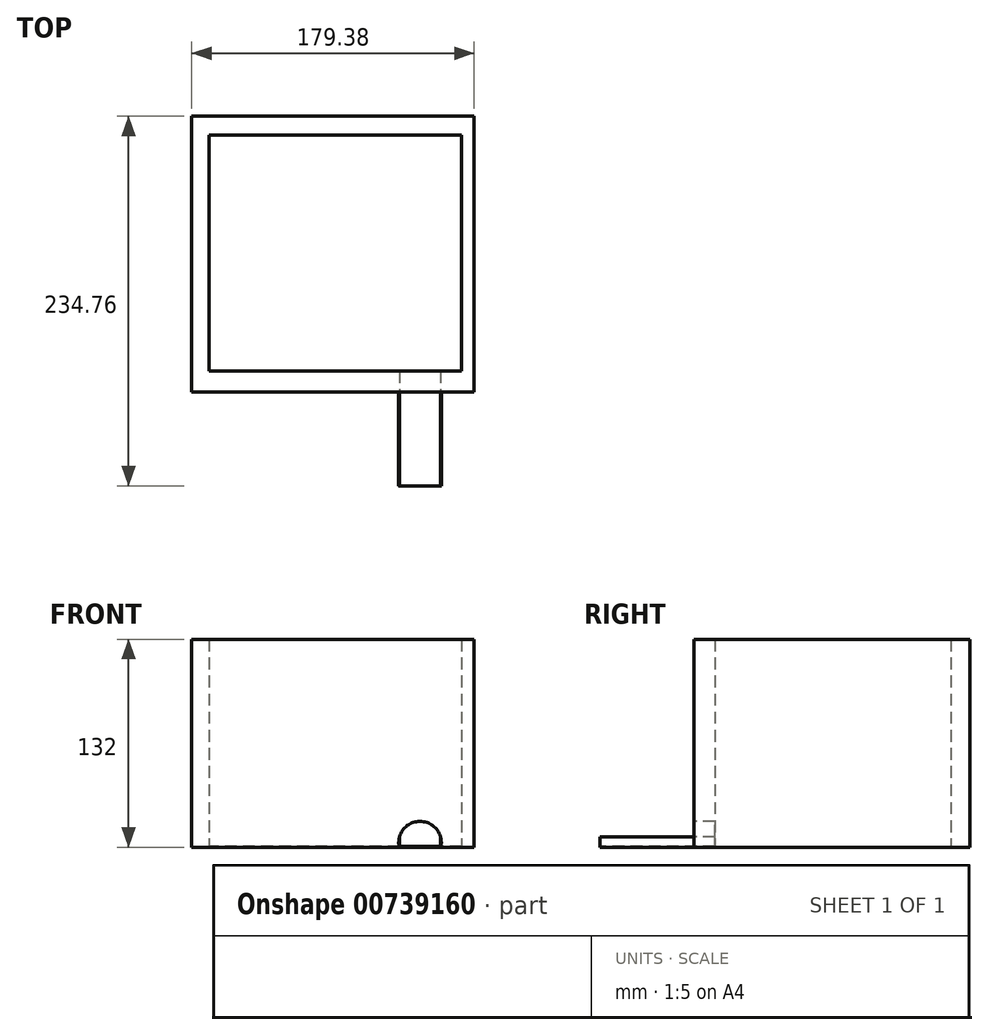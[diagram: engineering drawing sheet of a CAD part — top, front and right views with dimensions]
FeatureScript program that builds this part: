
annotation { "Feature Type Name" : "Feature", "Feature Type Description" : "" }
export const myFeature = defineFeature(function(context is Context, id is Id, definition is map)
    precondition{}
    {
        {
            var Q0;
            Q0=qCreatedBy(makeId("Top.planeOp"),FACE);
            var sketch = newSketch(context, id + "F0", { "sketchPlane" : qUnion([Q0])});
            skLineSegment(sketch, "E0.bottom", {"start": v(-79.21, -70.61) * mm, "end": v(100.17, -70.61) * mm});
            skLineSegment(sketch, "E0.top", {"start": v(-79.21, 104.46) * mm, "end": v(100.17, 104.46) * mm});
            skLineSegment(sketch, "E0.left", {"start": v(-79.21, -70.61) * mm, "end": v(-79.21, 104.46) * mm});
            skLineSegment(sketch, "E0.right", {"start": v(100.17, -70.61) * mm, "end": v(100.17, 104.46) * mm});
            skLineSegment(sketch, "E1.bottom", {"start": v(-68.23, -54.4) * mm, "end": v(92.28, -54.4) * mm});
            skLineSegment(sketch, "E1.top", {"start": v(-68.23, 92.5) * mm, "end": v(92.28, 92.5) * mm});
            skLineSegment(sketch, "E1.left", {"start": v(-68.23, -54.4) * mm, "end": v(-68.23, 92.5) * mm});
            skLineSegment(sketch, "E1.right", {"start": v(92.28, -54.4) * mm, "end": v(92.28, 92.5) * mm});
            skSolve(sketch);
        }
        {
            var Q0;
            Q0=makeQuery(id+"F0.imprint","IMPRINT",FACE,{"disambiguationData":[TD([[makeQuery(id+"F0.imprint","IMPRINT",EDGE,{"derivedFrom":sQuery(id+"F0.wireOp",EDGE,"E0.bottom")}),1.0]])]});
            extrude(context, id + "F1", {"entities" : qUnion([Q0]), "depth" : 132 * mm, "offsetDistance" : 25 * mm});
        }
        {
            var Q0;
            Q0=makeQuery(id+"F1.opExtrude","SWEPT_FACE",FACE,{"disambiguationData":[OSD([sQuery(id+"F0.wireOp",EDGE,"E0.bottom")])]});
            var sketch = newSketch(context, id + "F2", { "sketchPlane" : qUnion([Q0])});
            skArc(sketch, "E2", {"start": v(78.99, 0) * mm, "mid": v(65.79, 16.4) * mm, "end": v(52.59, 0) * mm});
            skSolve(sketch);
        }
        {
            var Q0;
            {var subQ0=sQuery(id+"F2.wireOp",EDGE,"E2");Q0=makeQuery(id+"F2.imprint","IMPRINT",FACE,{"disambiguationData":[TD([[makeQuery(id+"F2.imprint","IMPRINT",EDGE,{"derivedFrom":subQ0}),1.0]])]});}
            extrude(context, id + "F3", {"entities" : qUnion([Q0]), "operationType" : NewBodyOperationType.REMOVE, "oppositeDirection" : true, "depth" : 25 * mm, "offsetDistance" : 25 * mm});
        }
        {
            var Q0;
            Q0=makeQuery(id+"F1.opExtrude","CAP_FACE",FACE,{"disambiguationData":[OSD([sQuery(id+"F0.wireOp",EDGE,"E0.bottom"),sQuery(id+"F0.wireOp",EDGE,"E0.top"),sQuery(id+"F0.wireOp",EDGE,"E0.left"),sQuery(id+"F0.wireOp",EDGE,"E0.right"),sQuery(id+"F0.wireOp",EDGE,"E1.bottom"),sQuery(id+"F0.wireOp",EDGE,"E1.top"),sQuery(id+"F0.wireOp",EDGE,"E1.left"),sQuery(id+"F0.wireOp",EDGE,"E1.right")])],"isStart":true});
            var sketch = newSketch(context, id + "F4", { "sketchPlane" : qUnion([Q0])});
            skLineSegment(sketch, "E3.bottom", {"start": v(-68.23, 54.4) * mm, "end": v(92.28, 54.4) * mm});
            skLineSegment(sketch, "E3.top", {"start": v(-68.23, -92.5) * mm, "end": v(92.28, -92.5) * mm});
            skLineSegment(sketch, "E3.left", {"start": v(-68.23, 54.4) * mm, "end": v(-68.23, -92.5) * mm});
            skLineSegment(sketch, "E3.right", {"start": v(92.28, 54.4) * mm, "end": v(92.28, -92.5) * mm});
            skSolve(sketch);
        }
        {
            var Q0;
            Q0=makeQuery(id+"F4.imprint","IMPRINT",FACE,{"disambiguationData":[TD([[makeQuery(id+"F4.imprint","IMPRINT",EDGE,{"derivedFrom":sQuery(id+"F4.wireOp",EDGE,"E3.top")}),1.0]])]});
            extrude(context, id + "F5", {"entities" : qUnion([Q0]), "operationType" : NewBodyOperationType.ADD, "oppositeDirection" : true, "depth" : 10 * mm, "offsetDistance" : 25 * mm});
        }
        {
            var Q0;
            Q0=makeQuery(id+"F5.opExtrude","CAP_FACE",FACE,{"disambiguationData":[OSD([sQuery(id+"F4.wireOp",EDGE,"E3.bottom"),sQuery(id+"F4.wireOp",EDGE,"E3.top"),sQuery(id+"F4.wireOp",EDGE,"E3.left"),sQuery(id+"F4.wireOp",EDGE,"E3.right")])],"isStart":false});
            extrude(context, id + "F6", {"entities" : qUnion([Q0]), "operationType" : NewBodyOperationType.REMOVE, "oppositeDirection" : true, "depth" : 10 * mm, "offsetDistance" : 25 * mm});
        }
        {
            var Q0;
            Q0=makeQuery(id+"F6.boolean.opBoolean","MERGE",FACE,{"derivedFrom":[makeQuery(id+"F1.opExtrude","SWEPT_FACE",FACE,{"disambiguationData":[OSD([sQuery(id+"F0.wireOp",EDGE,"E1.top")])]}),makeQuery(id+"F6.opExtrude","SWEPT_FACE",FACE,{"disambiguationData":[OSD([sQuery(id+"F4.wireOp",EDGE,"E3.top")])]})]});
            var sketch = newSketch(context, id + "F7", { "sketchPlane" : qUnion([Q0])});
            skLineSegment(sketch, "E4", {"start": v(92.28, 6.67) * mm, "end": v(-68.23, 6.67) * mm});
            skSolve(sketch);
        }
        {
            var Q0;
            Q0 = qSketchRegion(id + "F7", true);
            var Q1;
            {var subQ0=sQuery(id+"F7.wireOp",EDGE,"E4");Q1=makeQuery(id+"F7.imprint","IMPRINT",FACE,{"disambiguationData":[TD([[makeQuery(id+"F7.imprint","IMPRINT",EDGE,{"derivedFrom":subQ0}),1.0]])]});}
            extrude(context, id + "F8", {"entities" : qUnion([Q0, Q1]), "operationType" : NewBodyOperationType.ADD, "depth" : 163 * mm, "offsetDistance" : 25 * mm});
        }
        {
            var Q0;
            Q0=makeQuery(id+"F8.opExtrude","SWEPT_FACE",FACE,{"disambiguationData":[OSD([sQuery(id+"F7.wireOp",EDGE,"E4")])]});
            extrude(context, id + "F9", {"entities" : qUnion([Q0]), "operationType" : NewBodyOperationType.REMOVE, "oppositeDirection" : true, "depth" : 6 * mm, "offsetDistance" : 25 * mm});
        }
        {
            var Q0;
            {var subQ0=sQuery(id+"F7.wireOp",EDGE,"E4");var subQ1=makeQuery(id+"F8.opExtrude","SWEPT_FACE",FACE,{"disambiguationData":[OSD([subQ0])]});var subQ2=sQuery(id+"F4.wireOp",EDGE,"E3.bottom");var subQ3=sQuery(id+"F0.wireOp",EDGE,"E1.bottom");var subQ4=makeQuery(id+"F6.boolean.opBoolean","MERGE",FACE,{"derivedFrom":[makeQuery(id+"F1.opExtrude","SWEPT_FACE",FACE,{"disambiguationData":[OSD([subQ3])]}),makeQuery(id+"F6.opExtrude","SWEPT_FACE",FACE,{"disambiguationData":[OSD([subQ2])]})]});Q0=makeQuery(id+"F9.boolean.opBoolean","MERGE",FACE,{"derivedFrom":[subQ4,makeQuery(id+"F9.opExtrude","SWEPT_FACE",FACE,{"disambiguationData":[OSD([subQ3,subQ2,subQ0]),TDD([makeQuery(id+"F8.boolean.opBoolean","INTERSECT",EDGE,{"disambiguationData":[OD(0.0)],"derivedFrom":[subQ4,subQ1]})])]}),makeQuery(id+"F9.opExtrude","SWEPT_FACE",FACE,{"disambiguationData":[OSD([subQ3,subQ2,subQ0]),TDD([makeQuery(id+"F8.boolean.opBoolean","INTERSECT",EDGE,{"disambiguationData":[OD(1.0)],"derivedFrom":[subQ4,subQ1]})])]})]});}
            extrude(context, id + "F10", {"entities" : qUnion([Q0]), "operationType" : NewBodyOperationType.REMOVE, "oppositeDirection" : true, "depth" : 3 * mm, "offsetDistance" : 25 * mm});
        }
        {
            var Q0;
            Q0=makeQuery(id+"F8.opExtrude","CAP_FACE",FACE,{"disambiguationData":[OSD([sQuery(id+"F0.wireOp",EDGE,"E1.top"),sQuery(id+"F0.wireOp",EDGE,"E1.left"),sQuery(id+"F0.wireOp",EDGE,"E1.right"),sQuery(id+"F4.wireOp",EDGE,"E3.top"),sQuery(id+"F4.wireOp",EDGE,"E3.left"),sQuery(id+"F4.wireOp",EDGE,"E3.right"),sQuery(id+"F7.wireOp",EDGE,"E4")])],"isStart":false});
            extrude(context, id + "F11", {"entities" : qUnion([Q0]), "operationType" : NewBodyOperationType.ADD, "depth" : 59.8 * mm, "offsetDistance" : 25 * mm});
        }
    });
